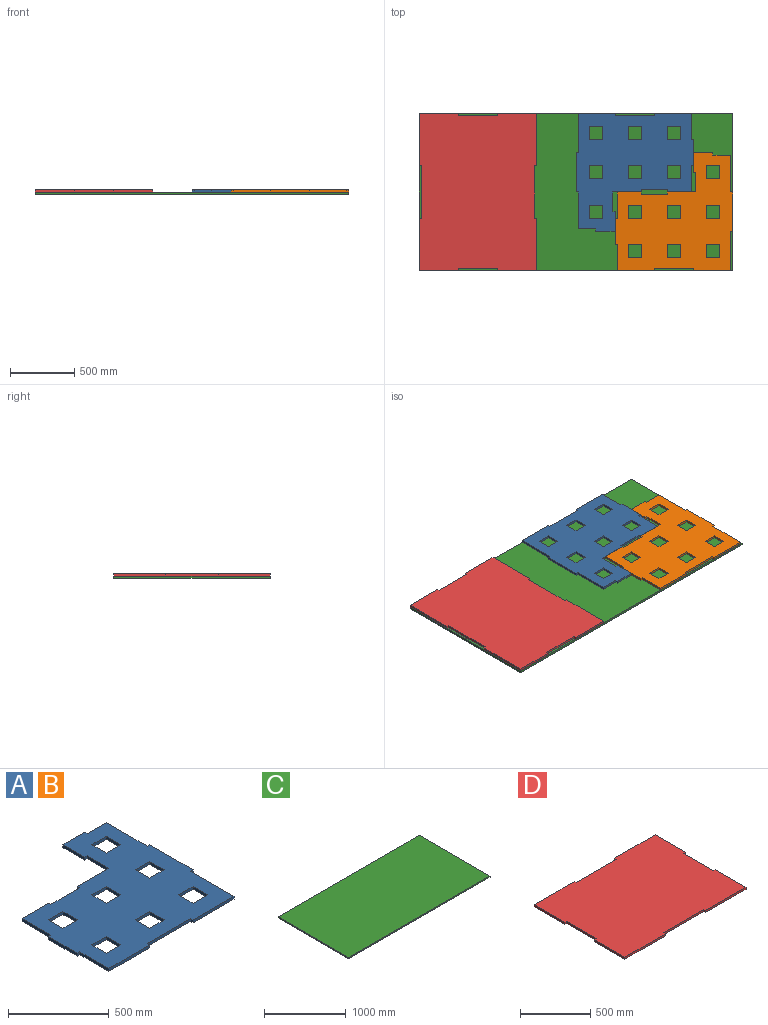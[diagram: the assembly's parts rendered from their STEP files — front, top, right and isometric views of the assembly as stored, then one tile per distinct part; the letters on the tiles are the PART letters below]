
ASSEMBLY  parts=4 mates=3
PART A: 56 faces, bbox 914.4x914.4x17.5 mm
  f0: plane 914.4x914.4mm, normal (0,0,1), area 546657.2mm2, adj f2,f3,f4,f5,f6,f7,f8,f9
  f1: plane 914.4x914.4mm, normal (0,0,-1), area 546657.2mm2, adj f2,f3,f4,f5,f6,f7,f8,f9
  f2: plane 304.8x17.46mm, normal (0,-1,0), area 5322.6mm2, adj f0,f1,f3,f27
  f3: plane 17.46x17.46mm, normal (-1,0,0), area 304.9mm2, adj f0,f1,f2,f4
  f4: plane 287.34x17.46mm, normal (0,-1,0), area 5017.6mm2, adj f0,f1,f3,f5
  f5: plane 304.8x17.46mm, normal (1,0,0), area 5322.6mm2, adj f0,f1,f4,f6
  f6: plane 17.46x17.46mm, normal (0,-1,0), area 304.9mm2, adj f0,f1,f5,f7
  f7: plane 304.8x17.46mm, normal (1,0,0), area 5322.6mm2, adj f0,f1,f6,f8
  f8: plane 17.46x17.46mm, normal (0,1,0), area 304.9mm2, adj f0,f1,f7,f9
  f9: plane 287.34x17.46mm, normal (1,0,0), area 5017.6mm2, adj f0,f1,f8,f10
  f10: plane 134.94x17.46mm, normal (0,1,0), area 2356.3mm2, adj f0,f1,f9,f11
  f11: plane 17.46x17.46mm, normal (1,0,0), area 304.9mm2, adj f0,f1,f10,f12
  f12: plane 152.4x17.46mm, normal (0,1,0), area 2661.3mm2, adj f0,f1,f11,f13
  f13: plane 152.4x17.46mm, normal (-1,0,0), area 2661.3mm2, adj f0,f1,f12,f14
  f14: plane 17.46x17.46mm, normal (0,-1,0), area 304.9mm2, adj f0,f1,f13,f15
  f15: plane 152.4x17.46mm, normal (-1,0,0), area 2661.3mm2, adj f0,f1,f14,f16
  f16: plane 220.66x17.46mm, normal (0,1,0), area 3853.3mm2, adj f0,f1,f15,f17
  f17: plane 17.46x16.36mm, normal (-1,0,0), area 285.7mm2, adj f0,f1,f16,f18
  f18: plane 203.2x17.46mm, normal (0,1,0), area 3548.4mm2, adj f0,f1,f17,f19
  f19: plane 17.46x16.36mm, normal (1,0,0), area 285.7mm2, adj f0,f1,f18,f20
  f20: plane 185.74x17.46mm, normal (0,1,0), area 3243.4mm2, adj f0,f1,f19,f21
  f21: plane 203.2x17.46mm, normal (-1,0,0), area 3548.4mm2, adj f0,f1,f20,f22
  f22: plane 17.46x17.46mm, normal (0,1,0), area 304.9mm2, adj f0,f1,f21,f23
  f23: plane 203.2x17.46mm, normal (-1,0,0), area 3548.4mm2, adj f0,f1,f22,f24
  f24: plane 17.46x17.46mm, normal (0,-1,0), area 304.9mm2, adj f0,f1,f23,f25
  f25: plane 203.2x17.46mm, normal (-1,0,0), area 3548.4mm2, adj f0,f1,f24,f26
  f26: plane 287.34x17.46mm, normal (0,-1,0), area 5017.6mm2, adj f0,f1,f25,f27
  f27: plane 17.46x17.46mm, normal (1,0,0), area 304.9mm2, adj f0,f1,f2,f26
  f28: plane 101.6x17.46mm, normal (-1,0,0), area 1774.2mm2, adj f0,f1,f29,f31
  f29: plane 101.6x17.46mm, normal (0,-1,0), area 1774.2mm2, adj f0,f1,f28,f30
  f30: plane 101.6x17.46mm, normal (1,0,0), area 1774.2mm2, adj f0,f1,f29,f31
  f31: plane 101.6x17.46mm, normal (0,1,0), area 1774.2mm2, adj f0,f1,f28,f30
  f32: plane 101.6x17.46mm, normal (-1,0,0), area 1774.2mm2, adj f0,f1,f33,f35
  f33: plane 101.6x17.46mm, normal (0,-1,0), area 1774.2mm2, adj f0,f1,f32,f34
  f34: plane 101.6x17.46mm, normal (1,0,0), area 1774.2mm2, adj f0,f1,f33,f35
  f35: plane 101.6x17.46mm, normal (0,1,0), area 1774.2mm2, adj f0,f1,f32,f34
  f36: plane 101.6x17.46mm, normal (-1,0,0), area 1774.2mm2, adj f0,f1,f37,f39
  f37: plane 101.6x17.46mm, normal (0,-1,0), area 1774.2mm2, adj f0,f1,f36,f38
  f38: plane 101.6x17.46mm, normal (1,0,0), area 1774.2mm2, adj f0,f1,f37,f39
  f39: plane 101.6x17.46mm, normal (0,1,0), area 1774.2mm2, adj f0,f1,f36,f38
  f40: plane 101.6x17.46mm, normal (-1,0,0), area 1774.2mm2, adj f0,f1,f41,f43
  f41: plane 101.6x17.46mm, normal (0,-1,0), area 1774.2mm2, adj f0,f1,f40,f42
  f42: plane 101.6x17.46mm, normal (1,0,0), area 1774.2mm2, adj f0,f1,f41,f43
  f43: plane 101.6x17.46mm, normal (0,1,0), area 1774.2mm2, adj f0,f1,f40,f42
  f44: plane 101.6x17.46mm, normal (-1,0,0), area 1774.2mm2, adj f0,f1,f45,f47
  f45: plane 101.6x17.46mm, normal (0,-1,0), area 1774.2mm2, adj f0,f1,f44,f46
  f46: plane 101.6x17.46mm, normal (1,0,0), area 1774.2mm2, adj f0,f1,f45,f47
  f47: plane 101.6x17.46mm, normal (0,1,0), area 1774.2mm2, adj f0,f1,f44,f46
  f48: plane 101.6x17.46mm, normal (-1,0,0), area 1774.2mm2, adj f0,f1,f49,f51
  f49: plane 101.6x17.46mm, normal (0,-1,0), area 1774.2mm2, adj f0,f1,f48,f50
  f50: plane 101.6x17.46mm, normal (1,0,0), area 1774.2mm2, adj f0,f1,f49,f51
  f51: plane 101.6x17.46mm, normal (0,1,0), area 1774.2mm2, adj f0,f1,f48,f50
  f52: plane 101.6x17.46mm, normal (0,-1,0), area 1774.2mm2, adj f0,f1,f53,f55
  f53: plane 101.6x17.46mm, normal (1,0,0), area 1774.2mm2, adj f0,f1,f52,f54
  f54: plane 101.6x17.46mm, normal (0,1,0), area 1774.2mm2, adj f0,f1,f53,f55
  f55: plane 101.6x17.46mm, normal (-1,0,0), area 1774.2mm2, adj f0,f1,f52,f54
PART B: same geometry as A
PART C: 6 faces, bbox 2438.4x1219.2x17.5 mm
  f0: plane 2438.4x17.46mm, normal (0,-1,0), area 42580.6mm2, adj f1,f3,f4,f5
  f1: plane 1219.2x17.46mm, normal (1,0,0), area 21290.3mm2, adj f0,f2,f4,f5
  f2: plane 2438.4x17.46mm, normal (0,1,0), area 42580.6mm2, adj f1,f3,f4,f5
  f3: plane 1219.2x17.46mm, normal (-1,0,0), area 21290.3mm2, adj f0,f2,f4,f5
  f4: plane 2438.4x1219.2mm, normal (0,0,1), area 2972897.3mm2, adj f0,f1,f2,f3
  f5: plane 2438.4x1219.2mm, normal (0,0,-1), area 2972897.3mm2, adj f0,f1,f2,f3
PART D: 22 faces, bbox 1219.2x914.4x17.5 mm
  f0: plane 17.46x17.46mm, normal (-1,0,0), area 304.9mm2, adj f1,f19,f20,f21
  f1: plane 406.4x17.46mm, normal (0,1,0), area 7096.8mm2, adj f0,f2,f20,f21
  f2: plane 17.46x17.46mm, normal (1,0,0), area 304.9mm2, adj f1,f3,f20,f21
  f3: plane 406.4x17.46mm, normal (0,1,0), area 7096.8mm2, adj f2,f4,f20,f21
  f4: plane 304.8x17.46mm, normal (-1,0,0), area 5322.6mm2, adj f3,f5,f20,f21
  f5: plane 17.46x17.46mm, normal (0,-1,0), area 304.9mm2, adj f4,f6,f20,f21
  f6: plane 304.8x17.46mm, normal (-1,0,0), area 5322.6mm2, adj f5,f7,f20,f21
  f7: plane 17.46x17.46mm, normal (0,1,0), area 304.9mm2, adj f6,f8,f20,f21
  f8: plane 304.8x17.46mm, normal (-1,0,0), area 5322.6mm2, adj f7,f9,f20,f21
  f9: plane 406.4x17.46mm, normal (0,-1,0), area 7096.8mm2, adj f8,f10,f20,f21
  f10: plane 17.46x17.46mm, normal (1,0,0), area 304.9mm2, adj f9,f11,f20,f21
  f11: plane 406.4x17.46mm, normal (0,-1,0), area 7096.8mm2, adj f10,f12,f20,f21
  f12: plane 17.46x17.46mm, normal (-1,0,0), area 304.9mm2, adj f11,f13,f20,f21
  f13: plane 406.4x17.46mm, normal (0,-1,0), area 7096.8mm2, adj f12,f14,f20,f21
  f14: plane 304.8x17.46mm, normal (1,0,0), area 5322.6mm2, adj f13,f15,f20,f21
  f15: plane 17.46x17.46mm, normal (0,1,0), area 304.9mm2, adj f14,f16,f20,f21
  f16: plane 304.8x17.46mm, normal (1,0,0), area 5322.6mm2, adj f15,f17,f20,f21
  f17: plane 17.46x17.46mm, normal (0,-1,0), area 304.9mm2, adj f16,f18,f20,f21
  f18: plane 304.8x17.46mm, normal (1,0,0), area 5322.6mm2, adj f17,f19,f20,f21
  f19: plane 406.4x17.46mm, normal (0,1,0), area 7096.8mm2, adj f0,f18,f20,f21
  f20: plane 1219.2x914.4mm, normal (0,0,1), area 1089997.8mm2, adj f0,f1,f2,f3,f4,f5,f6,f7
  f21: plane 1219.2x914.4mm, normal (0,0,-1), area 1089997.8mm2, adj f0,f1,f2,f3,f4,f5,f6,f7
PLACE A rot(axis=(0,0,-1),180deg) t=(455.63,-322.07,557.86)mm
PLACE B t=(-153.97,-322.07,557.86)mm
PLACE C t=(-458.77,-322.07,540.4)mm
PLACE D rot(axis=(0,0,1),90deg) t=(-1220.77,-322.07,557.86)mm
MATE fastened C.f4 <-> D.f21  axis (0,0,1) through (-1677.97,-931.67,557.86)mm
MATE fastened C.f4 <-> A.f1  axis (0,0,1) through (760.43,287.53,557.86)mm
MATE fastened B.f1 <-> C.f4  axis (0,0,-1) through (742.97,-931.67,557.86)mm
